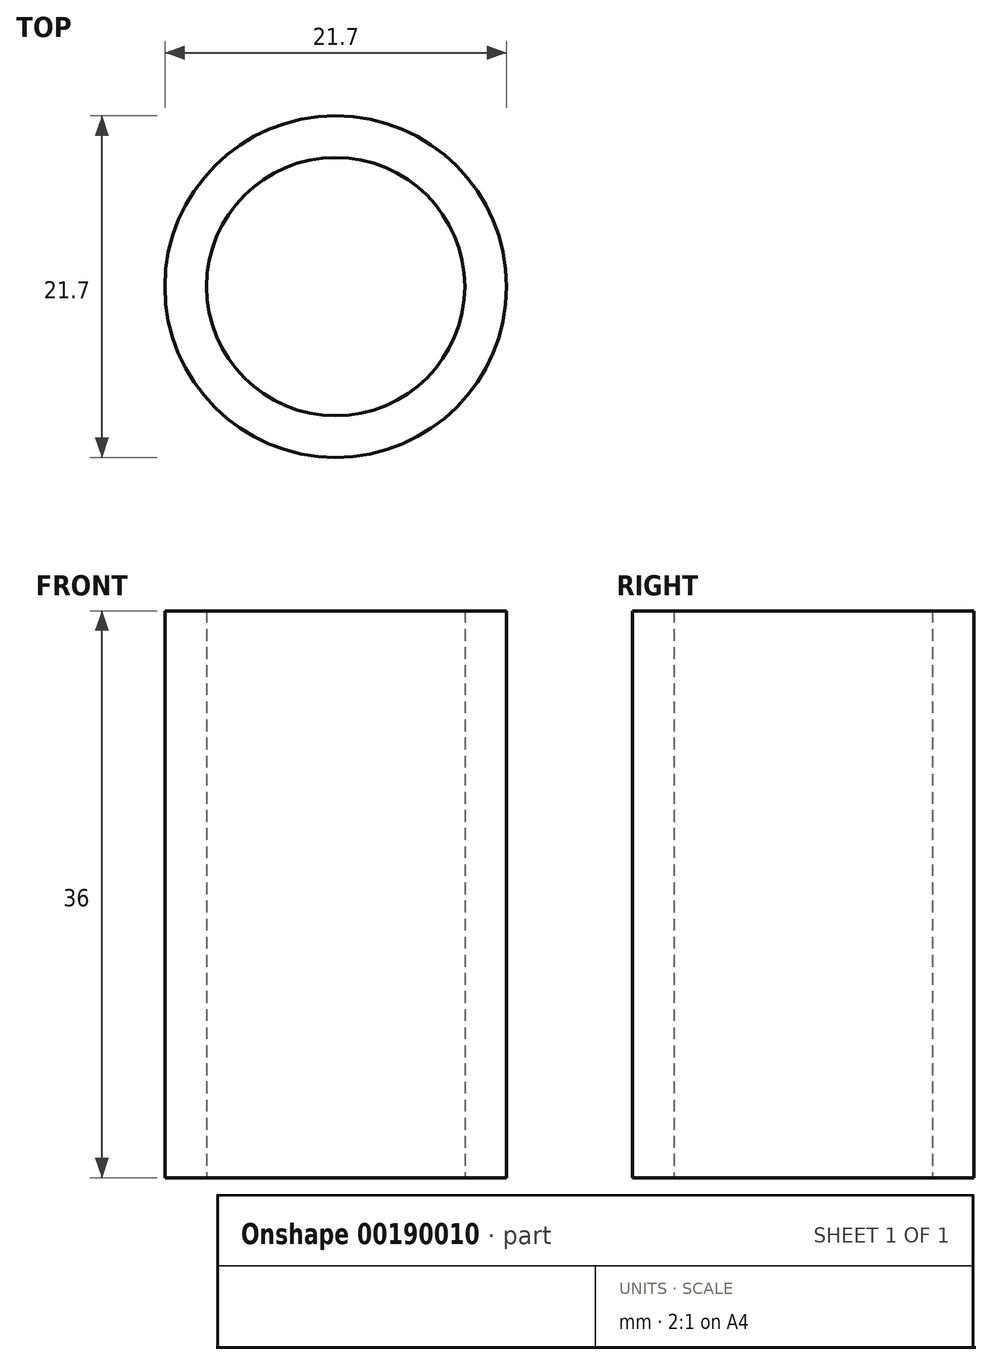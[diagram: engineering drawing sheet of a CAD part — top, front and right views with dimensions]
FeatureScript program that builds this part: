
annotation { "Feature Type Name" : "Feature", "Feature Type Description" : "" }
export const myFeature = defineFeature(function(context is Context, id is Id, definition is map)
    precondition{}
    {
        {
            var Q0;
            Q0=qCreatedBy(makeId("Top.planeOp"),FACE);
            var sketch = newSketch(context, id + "F0", { "sketchPlane" : qUnion([Q0])});
            skCircle(sketch, "E0", {"center": v(0, 0) * mm, "radius": 10.85 * mm});
            skCircle(sketch, "E1.0", {"center": v(0, 0) * mm, "radius": 8.2 * mm});
            skSolve(sketch);
        }
        {
            var Q0;
            Q0 = qSketchRegion(id + "F0", true);
            extrude(context, id + "F1", {"entities" : qUnion([Q0]), "depth" : 36 * mm});
        }
    });
